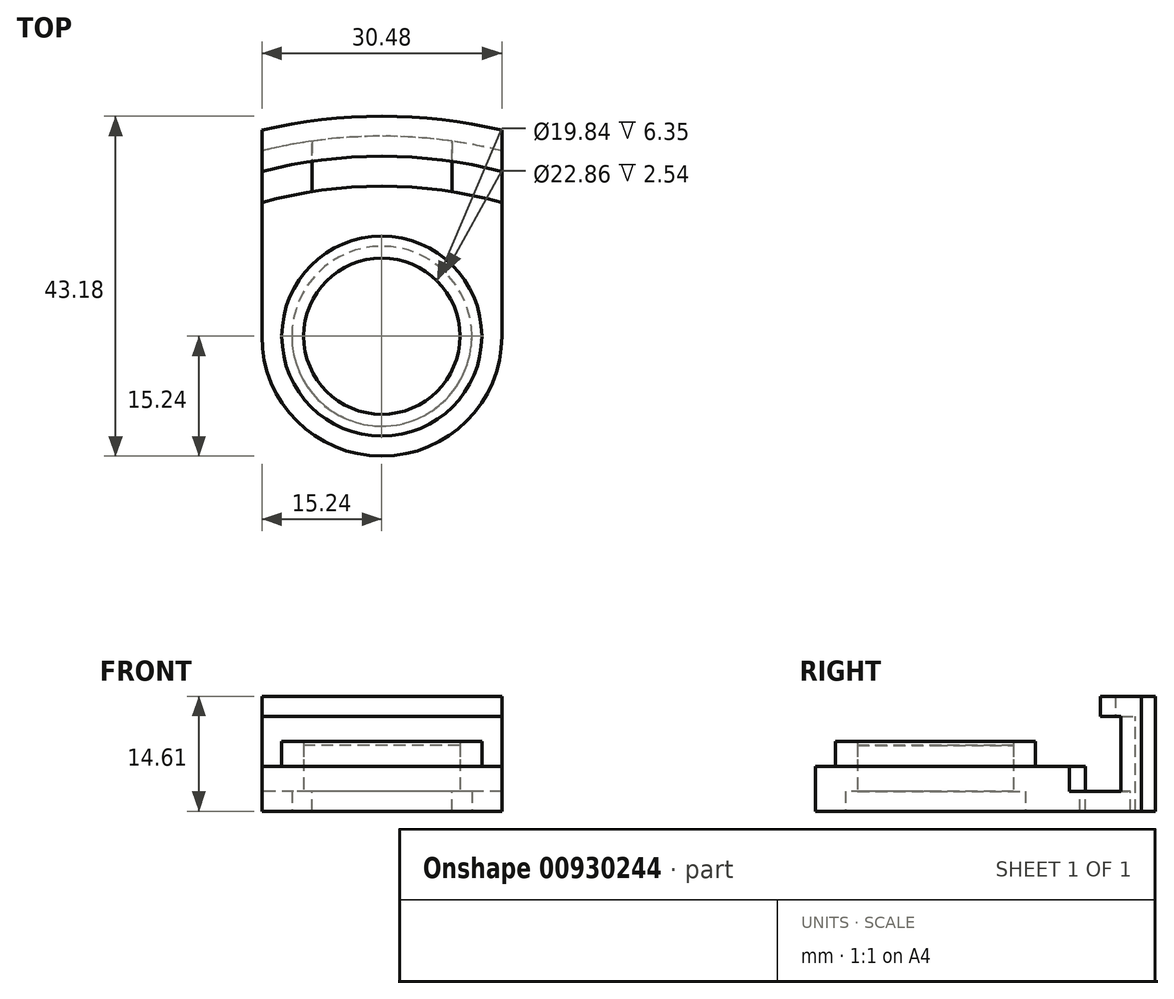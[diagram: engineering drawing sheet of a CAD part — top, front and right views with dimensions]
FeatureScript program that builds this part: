
annotation { "Feature Type Name" : "Feature", "Feature Type Description" : "" }
export const myFeature = defineFeature(function(context is Context, id is Id, definition is map)
    precondition{}
    {
        {
            var Q0;
            Q0=qCreatedBy(makeId("Top.planeOp"),FACE);
            var sketch = newSketch(context, id + "F0", { "sketchPlane" : qUnion([Q0])});
            skCircle(sketch, "E0", {"center": v(0, 0) * mm, "radius": 12.7 * mm});
            skCircle(sketch, "E1", {"center": v(0, 0) * mm, "radius": 9.92 * mm});
            skSolve(sketch);
        }
        {
            var Q0;
            Q0=makeQuery(id+"F0.imprint","IMPRINT",FACE,{"disambiguationData":[TD([[makeQuery(id+"F0.imprint","IMPRINT",EDGE,{"derivedFrom":sQuery(id+"F0.wireOp",EDGE,"E0")}),1.0]])]});
            extrude(context, id + "F1", {"entities" : qUnion([Q0]), "endBound" : BoundingType.SYMMETRIC, "depth" : 6.35 * mm, "offsetDistance" : 25.4 * mm});
        }
        {
            var Q0;
            Q0=makeQuery(id+"F0.imprint","IMPRINT",FACE,{"disambiguationData":[TD([[makeQuery(id+"F0.imprint","IMPRINT",EDGE,{"derivedFrom":sQuery(id+"F0.wireOp",EDGE,"E1")}),1.0]])]});
            extrude(context, id + "F2", {"entities" : qUnion([Q0]), "depth" : 2.67 * mm, "offsetDistance" : 25.4 * mm});
        }
        {
            var Q0;
            Q0=qCreatedBy(makeId("Top.planeOp"),FACE);
            var sketch = newSketch(context, id + "F3", { "sketchPlane" : qUnion([Q0])});
            skArc(sketch, "E2", {"start": v(-15.24, 0) * mm, "mid": v(0, -15.24) * mm, "end": v(15.24, 0) * mm});
            skLineSegment(sketch, "E3.bottom", {"start": v(-15.24, 0) * mm, "end": v(-12.7, 0) * mm});
            skLineSegment(sketch, "E3.top", {"start": v(-15.24, 16.98) * mm, "end": v(-12.7, 16.98) * mm});
            skLineSegment(sketch, "E3.left", {"start": v(-15.24, 0) * mm, "end": v(-15.24, 16.98) * mm});
            skLineSegment(sketch, "E3.right", {"start": v(-12.7, 0) * mm, "end": v(-12.7, 16.98) * mm});
            skLineSegment(sketch, "E4.bottom", {"start": v(15.24, 0) * mm, "end": v(12.7, 0) * mm});
            skLineSegment(sketch, "E4.top", {"start": v(15.24, 16.98) * mm, "end": v(12.7, 16.98) * mm});
            skLineSegment(sketch, "E4.left", {"start": v(15.24, 0) * mm, "end": v(15.24, 16.98) * mm});
            skLineSegment(sketch, "E4.right", {"start": v(12.7, 0) * mm, "end": v(12.7, 16.98) * mm});
            skArc(sketch, "E5", {"start": v(-12.7, 0) * mm, "mid": v(0, -12.7) * mm, "end": v(12.7, 0) * mm});
            skArc(sketch, "E6", {"start": v(15.24, 16.98) * mm, "mid": v(0, 19.05) * mm, "end": v(-15.24, 16.98) * mm});
            skCircle(sketch, "E7.0.0", {"center": v(0, 0) * mm, "radius": 12.7 * mm});
            skSolve(sketch);
        }
        {
            var Q0;
            Q0=makeQuery(id+"F3.imprint","IMPRINT",FACE,{"disambiguationData":[TD([[makeQuery(id+"F3.imprint","IMPRINT",EDGE,{"derivedFrom":sQuery(id+"F3.wireOp",EDGE,"E4.bottom")}),-1.0]])]});
            var Q1;
            Q1=makeQuery(id+"F3.imprint","IMPRINT",FACE,{"disambiguationData":[TD([[makeQuery(id+"F3.imprint","IMPRINT",EDGE,{"derivedFrom":sQuery(id+"F3.wireOp",EDGE,"E2")}),1.0]])]});
            var Q2;
            Q2=makeQuery(id+"F3.imprint","IMPRINT",FACE,{"disambiguationData":[TD([[makeQuery(id+"F3.imprint","IMPRINT",EDGE,{"derivedFrom":sQuery(id+"F3.wireOp",EDGE,"E3.bottom")}),1.0]])]});
            var Q3;
            Q3=makeQuery(id+"F3.imprint","IMPRINT",FACE,{"disambiguationData":[TD([[makeQuery(id+"F3.imprint","IMPRINT",EDGE,{"derivedFrom":sQuery(id+"F3.wireOp",EDGE,"E3.top")}),1.0]])]});
            extrude(context, id + "F4", {"entities" : qUnion([Q0, Q1, Q2, Q3]), "oppositeDirection" : true, "depth" : 5.7 * mm, "offsetDistance" : 25.4 * mm});
        }
        {
            var Q0;
            Q0=makeQuery(id+"F4.opExtrude","CAP_FACE",FACE,{"disambiguationData":[OSD([sQuery(id+"F3.wireOp",EDGE,"E2"),sQuery(id+"F3.wireOp",EDGE,"E3.left"),sQuery(id+"F3.wireOp",EDGE,"E4.left"),sQuery(id+"F3.wireOp",EDGE,"E6"),sQuery(id+"F3.wireOp",EDGE,"E7.0.0")])],"isStart":false});
            var sketch = newSketch(context, id + "F5", { "sketchPlane" : qUnion([Q0])});
            skCircle(sketch, "E8", {"center": v(0, 0) * mm, "radius": 11.43 * mm});
            skArc(sketch, "E9.0.0", {"start": v(15.24, 0) * mm, "mid": v(0, 15.24) * mm, "end": v(-15.24, 0) * mm});
            skLineSegment(sketch, "E9.0.1", {"start": v(-15.24, 0) * mm, "end": v(-15.24, -16.98) * mm});
            skArc(sketch, "E9.0.2", {"start": v(-15.24, -16.98) * mm, "mid": v(0, -19.05) * mm, "end": v(15.24, -16.98) * mm});
            skLineSegment(sketch, "E9.0.3", {"start": v(15.24, -16.98) * mm, "end": v(15.24, 0) * mm});
            skSolve(sketch);
        }
        {
            var Q0;
            Q0=makeQuery(id+"F5.imprint","IMPRINT",FACE,{"disambiguationData":[TD([[makeQuery(id+"F5.imprint","IMPRINT",EDGE,{"derivedFrom":sQuery(id+"F5.wireOp",EDGE,"E8")}),-1.0]])]});
            extrude(context, id + "F6", {"entities" : qUnion([Q0]), "operationType" : NewBodyOperationType.ADD, "oppositeDirection" : true, "depth" : 2.54 * mm, "offsetDistance" : 25.4 * mm});
        }
        {
            var Q0;
            Q0=makeQuery(id+"F4.opExtrude","CAP_FACE",FACE,{"disambiguationData":[OSD([sQuery(id+"F3.wireOp",EDGE,"E2"),sQuery(id+"F3.wireOp",EDGE,"E3.left"),sQuery(id+"F3.wireOp",EDGE,"E4.left"),sQuery(id+"F3.wireOp",EDGE,"E6"),sQuery(id+"F3.wireOp",EDGE,"E7.0.0")])],"isStart":true});
            var sketch = newSketch(context, id + "F7", { "sketchPlane" : qUnion([Q0])});
            skArc(sketch, "E10", {"start": v(15.24, 23.54) * mm, "mid": v(0, 25.4) * mm, "end": v(-15.24, 23.54) * mm});
            skArc(sketch, "E11", {"start": v(15.24, 26.16) * mm, "mid": v(0, 27.94) * mm, "end": v(-15.24, 26.16) * mm});
            skLineSegment(sketch, "E12", {"start": v(-15.24, 26.16) * mm, "end": v(-15.24, 16.98) * mm});
            skLineSegment(sketch, "E13", {"start": v(15.24, 16.98) * mm, "end": v(15.24, 26.16) * mm});
            skLineSegment(sketch, "E14", {"start": v(8.89, 18.35) * mm, "end": v(8.89, 24.77) * mm});
            skLineSegment(sketch, "E15", {"start": v(-8.9, 24.77) * mm, "end": v(-8.9, 18.35) * mm});
            skSolve(sketch);
        }
        {
            var Q0;
            {var subQ3=sQuery(id+"F7.wireOp",EDGE,"E15");Q0=makeQuery(id+"F7.imprint","IMPRINT",FACE,{"disambiguationData":[TD([[makeQuery(id+"F7.imprint","IMPRINT",EDGE,{"derivedFrom":subQ3}),-1.0]])]});}
            var Q1;
            {var subQ0=sQuery(id+"F7.wireOp",EDGE,"E11");Q1=makeQuery(id+"F7.imprint","IMPRINT",FACE,{"disambiguationData":[TD([[makeQuery(id+"F7.imprint","IMPRINT",EDGE,{"derivedFrom":subQ0}),1.0]])]});}
            var Q2;
            {var subQ3=sQuery(id+"F7.wireOp",EDGE,"E14");Q2=makeQuery(id+"F7.imprint","IMPRINT",FACE,{"disambiguationData":[TD([[makeQuery(id+"F7.imprint","IMPRINT",EDGE,{"derivedFrom":subQ3}),-1.0]])]});}
            var Q3;
            {var subQ0=sQuery(id+"F3.wireOp",EDGE,"E7.0.0");Q3=makeQuery(id+"F6.boolean.opBoolean","MERGE",FACE,{"derivedFrom":[makeQuery(id+"F4.opExtrude","CAP_FACE",FACE,{"disambiguationData":[OSD([sQuery(id+"F3.wireOp",EDGE,"E2"),sQuery(id+"F3.wireOp",EDGE,"E3.left"),sQuery(id+"F3.wireOp",EDGE,"E4.left"),sQuery(id+"F3.wireOp",EDGE,"E6"),subQ0])],"isStart":false}),makeQuery(id+"F6.opExtrude","CAP_FACE",FACE,{"disambiguationData":[OSD([subQ0,sQuery(id+"F5.wireOp",EDGE,"E8")])],"isStart":true})]});}
            extrude(context, id + "F8", {"entities" : qUnion([Q0, Q1, Q2]), "operationType" : NewBodyOperationType.ADD, "endBound" : BoundingType.UP_TO_SURFACE, "oppositeDirection" : true, "depth" : 3.05 * mm, "endBoundEntityFace" : qUnion([Q3]), "offsetDistance" : 25.4 * mm});
        }
        {
            var Q0;
            {var subQ3=sQuery(id+"F7.wireOp",EDGE,"E15");Q0=makeQuery(id+"F7.imprint","IMPRINT",FACE,{"disambiguationData":[TD([[makeQuery(id+"F7.imprint","IMPRINT",EDGE,{"derivedFrom":subQ3}),-1.0]])]});}
            var Q1;
            {var subQ3=sQuery(id+"F7.wireOp",EDGE,"E14");Q1=makeQuery(id+"F7.imprint","IMPRINT",FACE,{"disambiguationData":[TD([[makeQuery(id+"F7.imprint","IMPRINT",EDGE,{"derivedFrom":subQ3}),-1.0]])]});}
            extrude(context, id + "F9", {"entities" : qUnion([Q0, Q1]), "operationType" : NewBodyOperationType.REMOVE, "oppositeDirection" : true, "depth" : 3.17 * mm, "offsetDistance" : 25.4 * mm});
        }
        {
            var Q0;
            {var subQ0=sQuery(id+"F7.wireOp",EDGE,"E11");var subQ1=sQuery(id+"F7.wireOp",EDGE,"E10");var subQ2=sQuery(id+"F7.wireOp",EDGE,"E12");var subQ3=sQuery(id+"F7.wireOp",EDGE,"E15");var subQ4=sQuery(id+"F3.wireOp",EDGE,"E4.left");var subQ5=sQuery(id+"F3.wireOp",EDGE,"E3.left");var subQ6=sQuery(id+"F7.wireOp",EDGE,"E13");var subQ7=sQuery(id+"F7.wireOp",EDGE,"E14");var subQ8=sQuery(id+"F3.wireOp",EDGE,"E6");Q0=makeQuery(id+"F9.boolean.opBoolean","SPLIT",FACE,{"disambiguationData":[TD([makeQuery(id+"F8.opExtrude","SWEPT_FACE",FACE,{"disambiguationData":[OSD([subQ1])]})])],"derivedFrom":makeQuery(id+"F8.boolean.opBoolean","MERGE",FACE,{"derivedFrom":[makeQuery(id+"F4.opExtrude","CAP_FACE",FACE,{"disambiguationData":[OSD([sQuery(id+"F3.wireOp",EDGE,"E2"),subQ5,subQ4,subQ8,sQuery(id+"F3.wireOp",EDGE,"E7.0.0")])],"isStart":true}),makeQuery(id+"F8.opExtrude","CAP_FACE",FACE,{"disambiguationData":[OSD([subQ8,subQ1,subQ0,subQ2,subQ6,subQ7,subQ3])],"isStart":true})]})});}
            extrude(context, id + "F10", {"entities" : qUnion([Q0]), "operationType" : NewBodyOperationType.ADD, "depth" : 6.35 * mm, "offsetDistance" : 25.4 * mm});
        }
        {
            var Q0;
            Q0=makeQuery(id+"F10.opExtrude","CAP_FACE",FACE,{"disambiguationData":[OSD([sQuery(id+"F3.wireOp",EDGE,"E2"),sQuery(id+"F3.wireOp",EDGE,"E3.left"),sQuery(id+"F3.wireOp",EDGE,"E4.left"),sQuery(id+"F3.wireOp",EDGE,"E6"),sQuery(id+"F3.wireOp",EDGE,"E7.0.0"),sQuery(id+"F7.wireOp",EDGE,"E10"),sQuery(id+"F7.wireOp",EDGE,"E11"),sQuery(id+"F7.wireOp",EDGE,"E12"),sQuery(id+"F7.wireOp",EDGE,"E13"),sQuery(id+"F7.wireOp",EDGE,"E14"),sQuery(id+"F7.wireOp",EDGE,"E15")])],"isStart":false});
            var sketch = newSketch(context, id + "F11", { "sketchPlane" : qUnion([Q0])});
            skArc(sketch, "E16", {"start": v(15.24, 20.92) * mm, "mid": v(0, 22.86) * mm, "end": v(-15.24, 20.92) * mm});
            skLineSegment(sketch, "E17", {"start": v(15.24, 23.54) * mm, "end": v(15.24, 20.92) * mm});
            skLineSegment(sketch, "E18", {"start": v(-15.24, 23.54) * mm, "end": v(-15.24, 20.92) * mm});
            skSolve(sketch);
        }
        {
            var Q0;
            Q0=makeQuery(id+"F11.imprint","IMPRINT",FACE,{"disambiguationData":[TD([[makeQuery(id+"F11.imprint","IMPRINT",EDGE,{"derivedFrom":makeQuery(id+"F10.opExtrude","CAP_EDGE",EDGE,{"disambiguationData":[OSD([sQuery(id+"F7.wireOp",EDGE,"E11")])],"isStart":false})}),1.0]])]});
            var Q1;
            Q1=makeQuery(id+"F11.imprint","IMPRINT",FACE,{"disambiguationData":[TD([[makeQuery(id+"F11.imprint","IMPRINT",EDGE,{"derivedFrom":sQuery(id+"F11.wireOp",EDGE,"E16")}),-1.0]])]});
            extrude(context, id + "F12", {"entities" : qUnion([Q0, Q1]), "operationType" : NewBodyOperationType.ADD, "depth" : 2.54 * mm, "offsetDistance" : 25.4 * mm});
        }
    });
